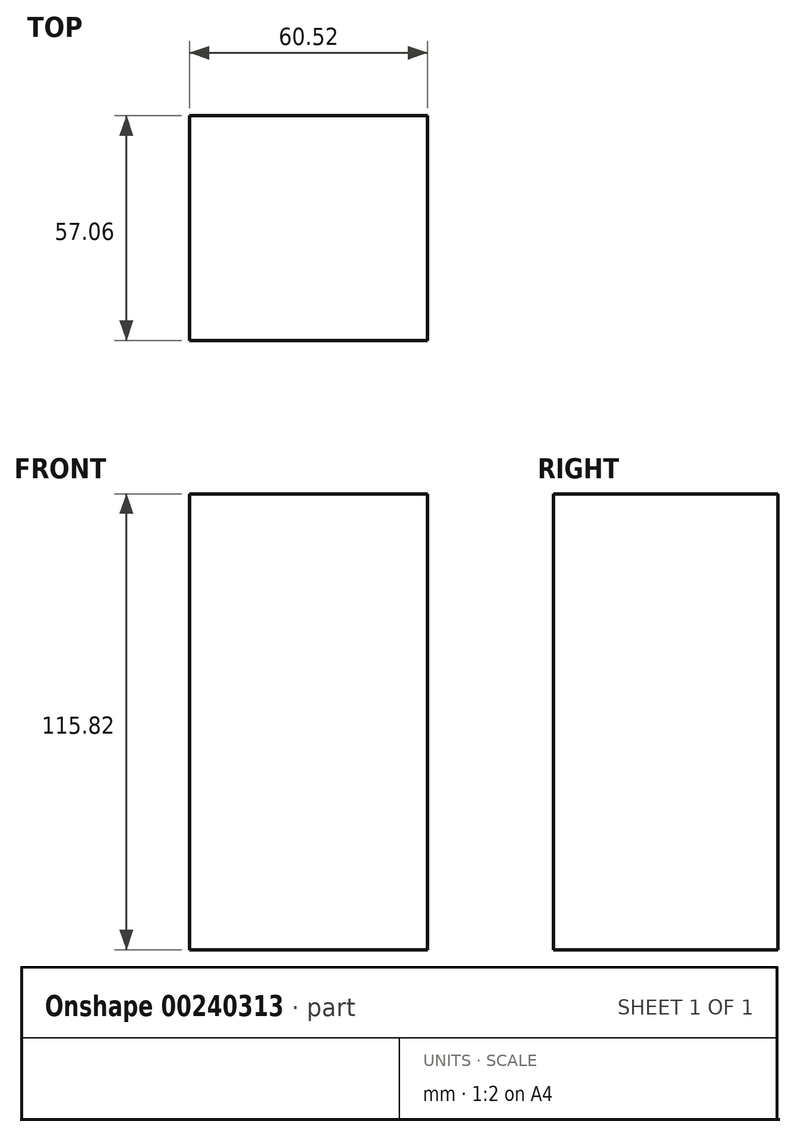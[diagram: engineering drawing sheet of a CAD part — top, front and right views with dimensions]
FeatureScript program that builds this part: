
annotation { "Feature Type Name" : "Feature", "Feature Type Description" : "" }
export const myFeature = defineFeature(function(context is Context, id is Id, definition is map)
    precondition{}
    {
        {
            var Q0;
            Q0=qCreatedBy(makeId("Top.planeOp"),FACE);
            var sketch = newSketch(context, id + "F0", { "sketchPlane" : qUnion([Q0])});
            skLineSegment(sketch, "E0.bottom", {"start": v(30.26, 28.53) * mm, "end": v(-30.26, 28.53) * mm});
            skLineSegment(sketch, "E0.top", {"start": v(30.26, -28.53) * mm, "end": v(-30.26, -28.53) * mm});
            skLineSegment(sketch, "E0.left", {"start": v(30.26, 28.53) * mm, "end": v(30.26, -28.53) * mm});
            skLineSegment(sketch, "E0.right", {"start": v(-30.26, 28.53) * mm, "end": v(-30.26, -28.53) * mm});
            skPoint(sketch, "E0.middle", {"position": v(0, 0) * mm});
            skSolve(sketch);
        }
        {
            var Q0;
            Q0 = qSketchRegion(id + "F0", true);
            extrude(context, id + "F1", {"entities" : qUnion([Q0]), "depth" : 115.82 * mm});
        }
    });
